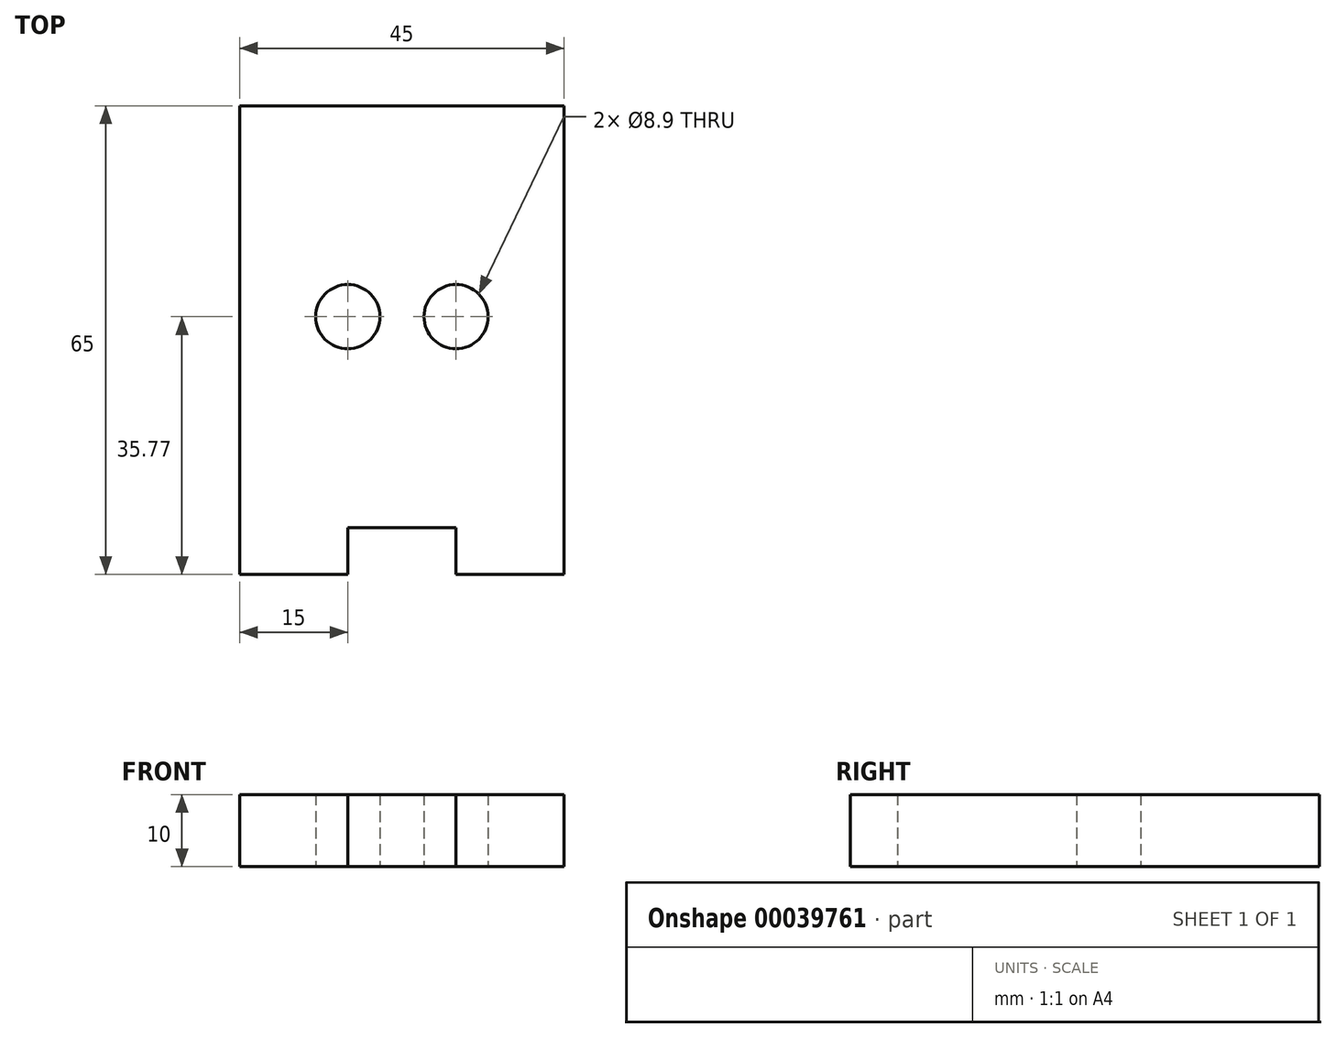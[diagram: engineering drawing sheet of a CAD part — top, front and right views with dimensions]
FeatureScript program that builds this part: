
annotation { "Feature Type Name" : "Feature", "Feature Type Description" : "" }
export const myFeature = defineFeature(function(context is Context, id is Id, definition is map)
    precondition{}
    {
        {
            var Q0;
            Q0=qCreatedBy(makeId("Top.planeOp"),FACE);
            var sketch = newSketch(context, id + "F0", { "sketchPlane" : qUnion([Q0])});
            skLineSegment(sketch, "E0.rect.bottom", {"start": v(-7.5, 29.23) * mm, "end": v(7.5, 29.23) * mm});
            skLineSegment(sketch, "E0.rect.top", {"start": v(-7.5, -29.23) * mm, "end": v(7.5, -29.23) * mm});
            skLineSegment(sketch, "E0.rect.left", {"start": v(-7.5, 29.23) * mm, "end": v(-7.5, -29.23) * mm});
            skLineSegment(sketch, "E0.rect.right", {"start": v(7.5, 29.23) * mm, "end": v(7.5, -29.23) * mm});
            skPoint(sketch, "E0.rect.middle", {"position": v(0, 0) * mm});
            skLineSegment(sketch, "E1.bottom", {"start": v(-7.5, 29.23) * mm, "end": v(-22.5, 29.23) * mm});
            skLineSegment(sketch, "E1.top", {"start": v(-7.5, -35.77) * mm, "end": v(-22.5, -35.77) * mm});
            skLineSegment(sketch, "E1.left", {"start": v(-7.5, 29.23) * mm, "end": v(-7.5, -35.77) * mm});
            skLineSegment(sketch, "E1.right", {"start": v(-22.5, 29.23) * mm, "end": v(-22.5, -35.77) * mm});
            skLineSegment(sketch, "E2.bottom", {"start": v(7.5, 29.23) * mm, "end": v(22.5, 29.23) * mm});
            skLineSegment(sketch, "E2.top", {"start": v(7.5, -35.77) * mm, "end": v(22.5, -35.77) * mm});
            skLineSegment(sketch, "E2.left", {"start": v(7.5, 29.23) * mm, "end": v(7.5, -35.77) * mm});
            skLineSegment(sketch, "E2.right", {"start": v(22.5, 29.23) * mm, "end": v(22.5, -35.77) * mm});
            skCircle(sketch, "E3", {"center": v(-7.5, 0) * mm, "radius": 4.45 * mm});
            skCircle(sketch, "E4", {"center": v(7.5, 0) * mm, "radius": 4.45 * mm});
            skSolve(sketch);
        }
        {
            var Q0;
            Q0 = qSketchRegion(id + "F0", true);
            extrude(context, id + "F1", {"entities" : qUnion([Q0]), "endBound" : BoundingType.SYMMETRIC, "depth" : 10 * mm});
        }
    });
